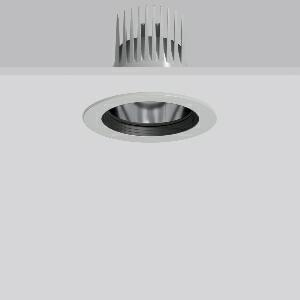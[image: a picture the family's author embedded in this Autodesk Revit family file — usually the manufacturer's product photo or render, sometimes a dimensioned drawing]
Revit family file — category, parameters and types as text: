
# Revit family: heledon_maxi_e_901757_004_2_4c54
name_source: partatom
category: Lighting Fixtures
units: mm (PartAtom-declared; Revit-internal decimal feet)

## family parameters
Cut with Voids When Loaded = No
Host = Face
Light Source = No
Part Type = Normal
Room Calculation Point = No
Round Connector Dimension = Use Diameter
Shared = No

## types (1)
- HELEDON maxi E (1 x LED Modul 927, 3150 lm, 2700)
    Apparent Load = 25 VA
    Approval mark = CE
    CIE Flux Codes = 100 100 100 100 100
    Color Rendering = 92
    Color Temperature = 2700
    Default Elevation = 1800 mm
    Description = Series: HELEDON maxi
Round recessed downlight. Housing: die-cast aluminium, powder-coated. Black plastic ring and recessed LED to prevent glare from the side. Optical assembly with reflector made of MIRO-Silver with 98% total light reflection for outstanding efficiency - can be changed without tools. Best colour rendering index Ra>90. Suitable for Recessed ceiling mounting. Installation without tools thanks to spring fastening system. Including separate LED converter with connecting cable 600 mm.High quality converter without flickering and stroboscopic effect. Through-wiring box (5 pole) available as accessory. The following accessories can be mounted without use of tools: interchangeable lenses, decorative glasses, honeycomb louvre, clear and frosted diffusers, white interchangeable plastic ring. 
Colour: silver
Diameter: 162 mm
Height: 3 mm
Cut-out diameter: 152 mm
Recess height: 200 mm
Luminaire: recess height: 135 mm
Lamp: LED
Socket: without socket
Colour temperature: 2700K
Colour rendering index (CRI): 92
System power: 25 W
Rated luminous flux: 3150 lm
Luminous efficiency: 126 lm/W
Control gear: Regulated power supply
Protection class: II
Type of protection: IP 20
    Height = 0 mm  [stored 0 ft]
    Lamp = 1 x LED Modul 927
    Lamp Light Flux = 3150 lm
    Lamp count = 1
    Length = 162 mm
    Lifetime = 50000 h
    Luminous efficacy = 126 lm/W
    Manufacturer = RZB
    ModVariant = No
    Model = 901757.004.2
    Mounting Place = Ceiling
    Mounting Type = Recessed
    Number of Poles = 1
    OnlyDefault = Yes
    Power Factor = 1
    Product Name = HELEDON maxi E
    Product group = Recessed downlights
    ProductGroupID = 402
    Protection Class = Protection class II
    Protection Degree = IP 20
    RLX_Detail_Level = 1
    RLX_Emergency_Light_Flux = 0 lm
    RLX_Emergency_Type = 0
    RLX_Emergency_Type_DB = No
    RlxData = <blob elided: 120185 chars, md5=dc352c08>
    Socket = socket
    Standby Power = 0 W
    System Light Flux = 3150 lm
    System Power = 25 W
    Type Comments = Product without accessories
    Type Image = 901662.004.jpg
    URL = http://relux.com
    VarID = ---
    Voltage = 230 V
    Voltage Range = 220-240 V
    Weight = 0.00 kg
    Width = 0 mm  [stored 0 ft]

note: [stored X ft] marks values corroborated as IEEE doubles in the binary element streams (Revit-internal decimal feet)

## geometry (parser evidence)
native form markers: Blend x4, Sweep x9
no freeform markers — native parametric forms only
